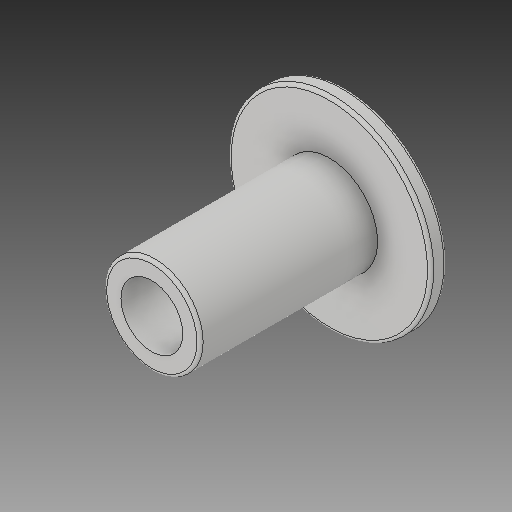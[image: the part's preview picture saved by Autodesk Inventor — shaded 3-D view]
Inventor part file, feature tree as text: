
AUTODESK INVENTOR PART (.ipt)
format: ipt  version: 2018 (Build 220112000, 112)  size: 147,456 bytes
history: native  units: in
note: dims shown in document units (in); Inventor stores cm internally (conversion verified against a paired STEP export)
features: fillet x1
ambient origin geometry x8: Origin, YZ Plane, XZ Plane, XY Plane, X Axis, Y Axis, Z Axis, Center Point
bodies: Solid1 (feature_tree)
feature tree (1):
  fillet  "Fillet2"  [1 undecoded]
note: 1 required parameter value undecoded (feature->parameter linkage not recoverable at this tier; creation-order binding heuristic only, values carry confidence <= 0.55)
